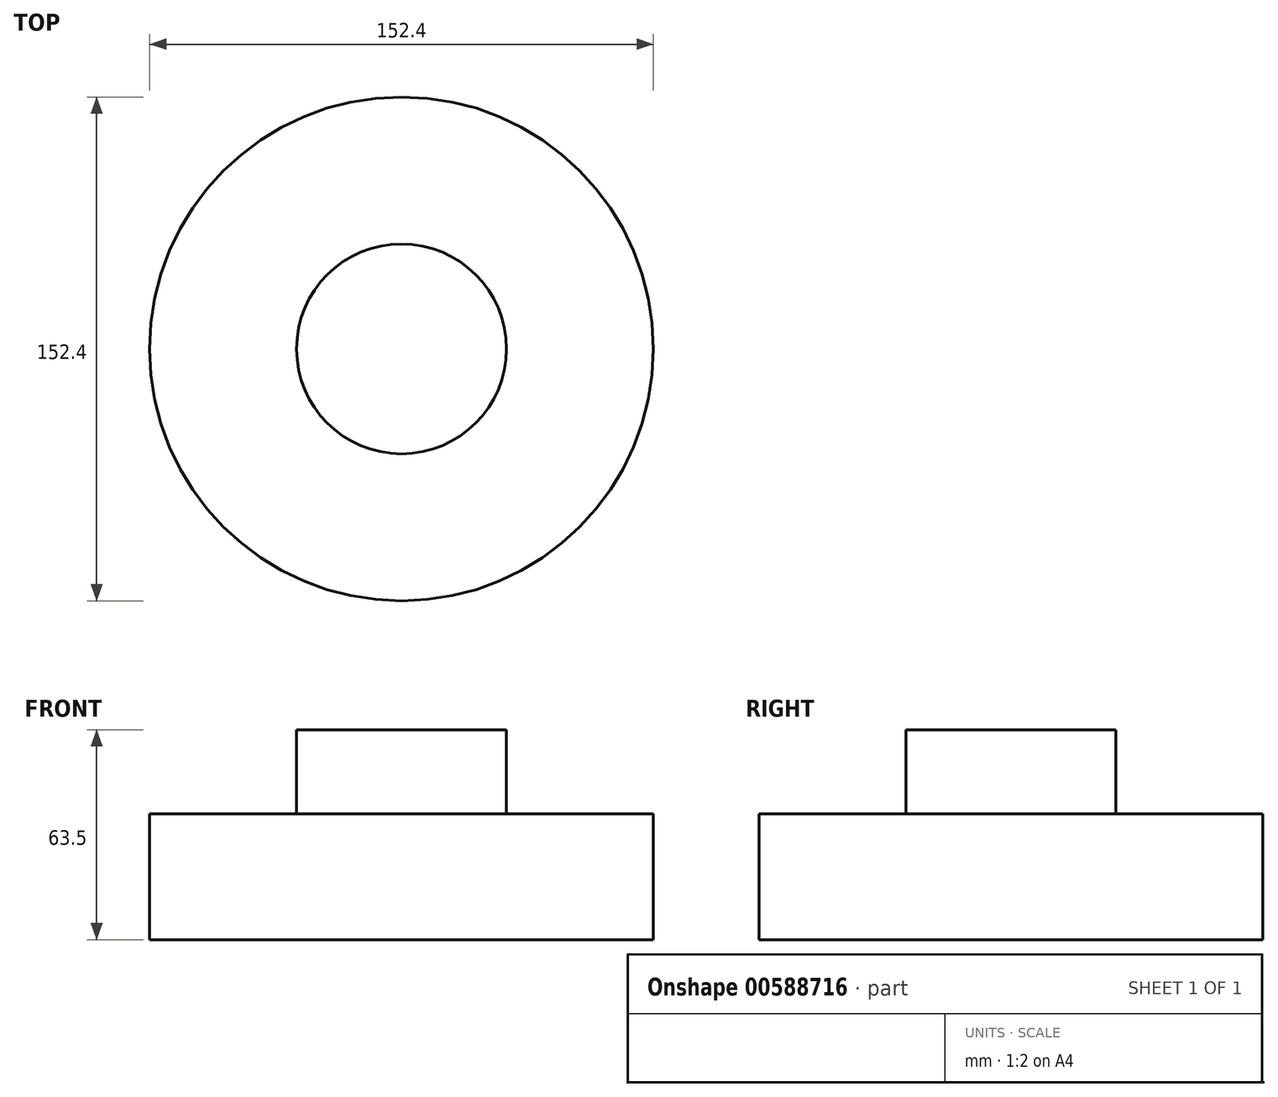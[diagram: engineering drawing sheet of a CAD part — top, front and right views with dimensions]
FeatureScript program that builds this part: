
annotation { "Feature Type Name" : "Feature", "Feature Type Description" : "" }
export const myFeature = defineFeature(function(context is Context, id is Id, definition is map)
    precondition{}
    {
        {
            var Q0;
            Q0=qCreatedBy(makeId("Front.planeOp"),FACE);
            var sketch = newSketch(context, id + "F0", { "sketchPlane" : qUnion([Q0])});
            skLineSegment(sketch, "E0", {"start": v(-95.25, 63.5) * mm, "end": v(-95.25, 0) * mm});
            skLineSegment(sketch, "E1", {"start": v(-95.25, 0) * mm, "end": v(-19.05, 0) * mm});
            skLineSegment(sketch, "E2", {"start": v(-19.05, 0) * mm, "end": v(-19.05, 38.1) * mm});
            skLineSegment(sketch, "E3", {"start": v(-19.05, 38.1) * mm, "end": v(-63.5, 38.1) * mm});
            skLineSegment(sketch, "E4", {"start": v(-63.5, 38.1) * mm, "end": v(-63.5, 63.5) * mm});
            skLineSegment(sketch, "E5", {"start": v(-95.25, 63.5) * mm, "end": v(-63.5, 63.5) * mm});
            skSolve(sketch);
        }
        {
            var Q0;
            Q0=makeQuery(id+"F0.imprint","IMPRINT",FACE,{"disambiguationData":[TD([[makeQuery(id+"F0.imprint","IMPRINT",EDGE,{"derivedFrom":sQuery(id+"F0.wireOp",EDGE,"E0")}),1.0]])]});
            var Q1;
            Q1 = qSketchRegion(id + "F0", true);
            var Q2;
            Q2=sQuery(id+"F0.wireOp",EDGE,"E0");
            revolve(context, id + "F1", {"entities" : qUnion([Q0, Q1]), "axis" : qUnion([Q2]), "revolveType" : RevolveType.FULL});
        }
    });
